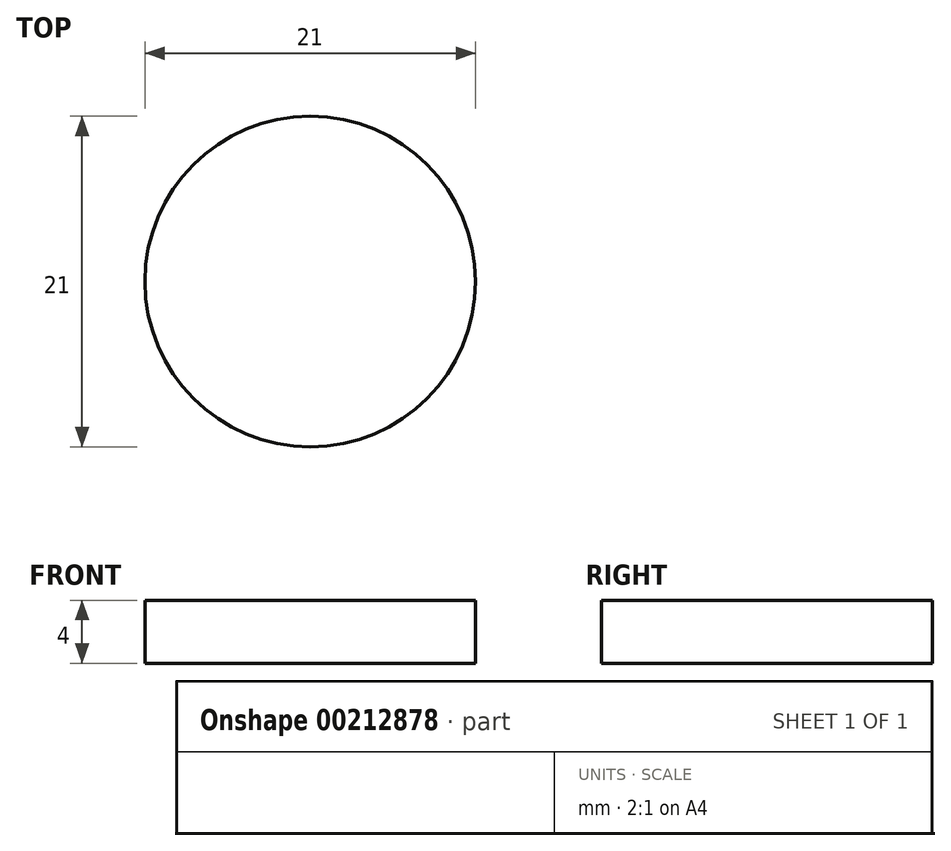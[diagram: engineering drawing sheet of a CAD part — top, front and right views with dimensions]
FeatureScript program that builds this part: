
annotation { "Feature Type Name" : "Feature", "Feature Type Description" : "" }
export const myFeature = defineFeature(function(context is Context, id is Id, definition is map)
    precondition{}
    {
        {
            var Q0;
            Q0=qCreatedBy(makeId("Top.planeOp"),FACE);
            var sketch = newSketch(context, id + "F0", { "sketchPlane" : qUnion([Q0])});
            skCircle(sketch, "E0", {"center": v(0, 0) * mm, "radius": 10.5 * mm});
            skSolve(sketch);
        }
        {
            var Q0;
            Q0 = qSketchRegion(id + "F0", true);
            extrude(context, id + "F1", {"entities" : qUnion([Q0]), "oppositeDirection" : true, "depth" : 4 * mm});
        }
    });
